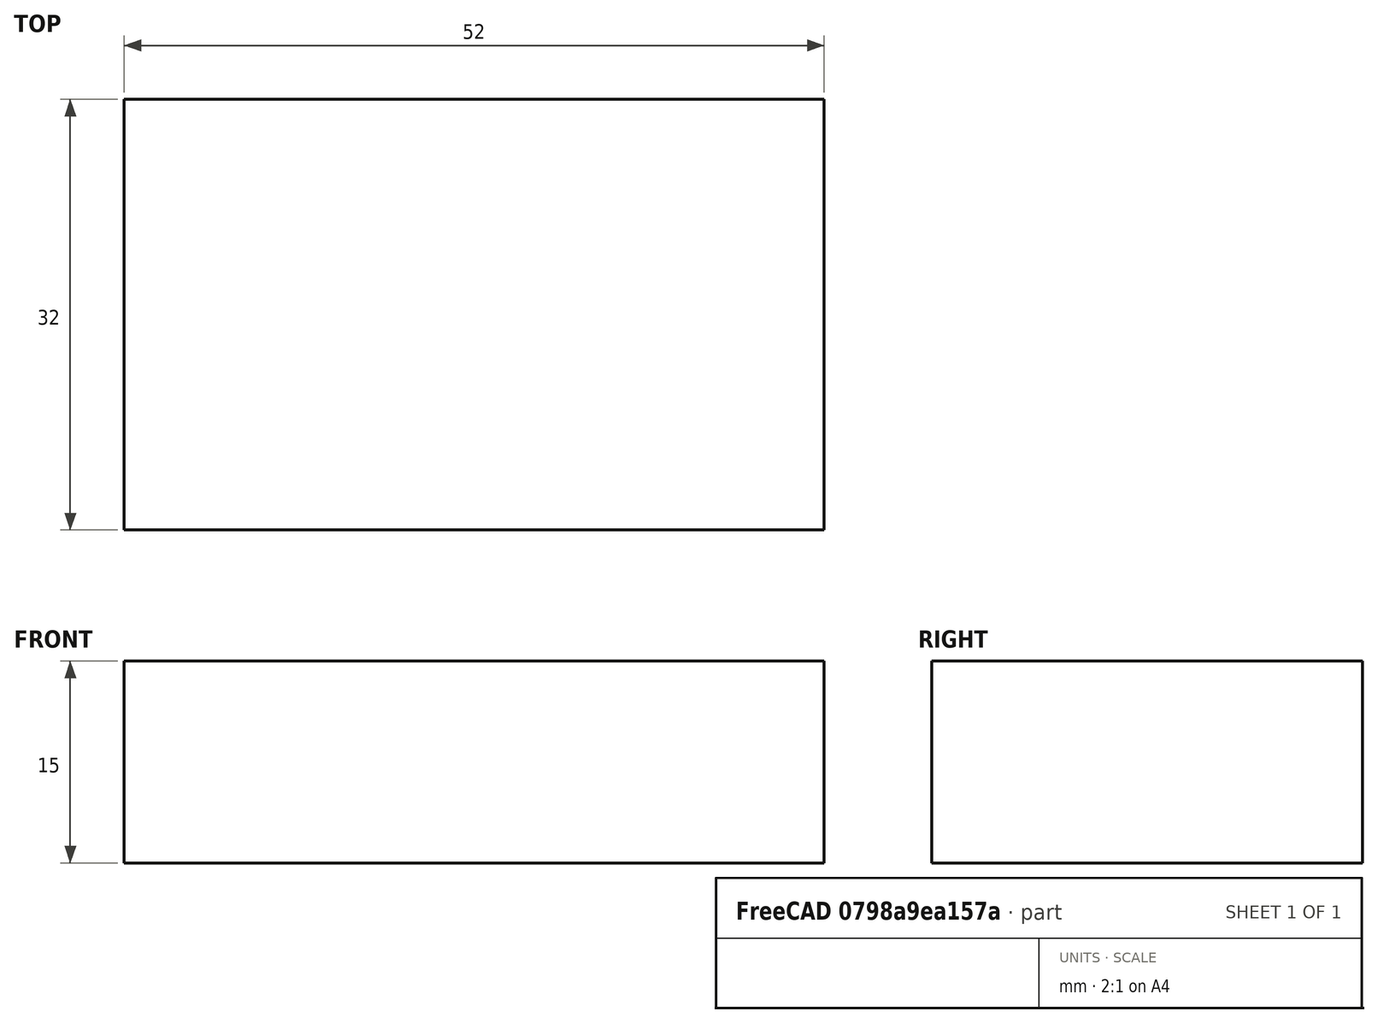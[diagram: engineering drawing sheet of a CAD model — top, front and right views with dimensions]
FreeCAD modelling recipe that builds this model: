
FCSTD DOCUMENT  (FreeCAD 0.19R)
Label: reely_receiver
License: All rights reserved
LicenseURL: http://en.wikipedia.org/wiki/All_rights_reserved
objects: Sketcher::SketchObject×1, PartDesign::Pad×1, PartDesign::Body×1
note: 4 computed .brp shape members not serialized (recipe doc carries the construction recipe); baked Part::Feature solids carry a one-line shape summary decoded from their .brp

FEATURE [Sketcher::SketchObject] Sketch
  MapMode = 5
  Support = -> [XY_Plane]
  sketch-geometry (4):
    g0: LineSegment StartX=0 StartY=0 StartZ=0 EndX=52 EndY=0 EndZ=0
    g1: LineSegment StartX=52 StartY=0 StartZ=0 EndX=52 EndY=32 EndZ=0
    g2: LineSegment StartX=52 StartY=32 StartZ=0 EndX=0 EndY=32 EndZ=0
    g3: LineSegment StartX=0 StartY=32 StartZ=0 EndX=0 EndY=0 EndZ=0
  constraints (11):
    c: Coincident(g0,g1)
    c: Coincident(g1,g2)
    c: Coincident(g2,g3)
    c: Coincident(g3,g0)
    c: Horizontal(g0)
    c: Horizontal(g2)
    c: Vertical(g1)
    c: Vertical(g3)
    c: Coincident(g0,g-1)
    c: DistanceX(g0,g0) = 52
    c: DistanceY(g1,g1) = 32
FEATURE [PartDesign::Pad] Pad
  Length = 15
  Length2 = 100
  Profile = -> Sketch
  Type = 0
FEATURE [PartDesign::Body] Body
  Group = -> [Sketch,Pad]
  Origin = -> Origin
  Tip = -> Pad
